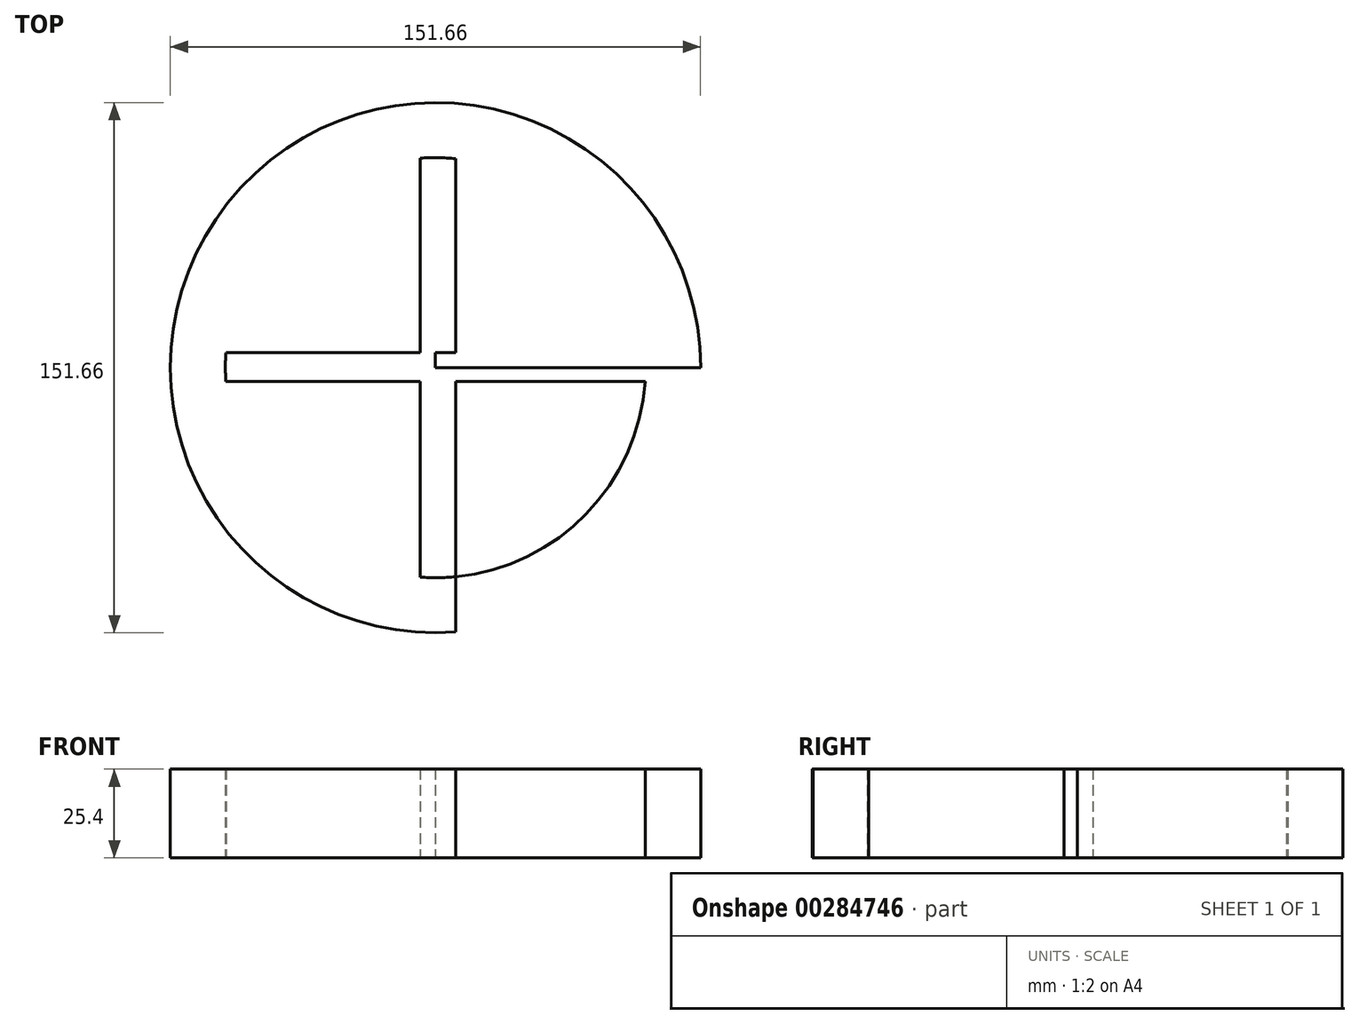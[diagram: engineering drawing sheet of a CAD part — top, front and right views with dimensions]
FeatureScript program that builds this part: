
annotation { "Feature Type Name" : "Feature", "Feature Type Description" : "" }
export const myFeature = defineFeature(function(context is Context, id is Id, definition is map)
    precondition{}
    {
        {
            var Q0;
            Q0=qCreatedBy(makeId("Top.planeOp"),FACE);
            var sketch = newSketch(context, id + "F0", { "sketchPlane" : qUnion([Q0])});
            skCircle(sketch, "E0", {"center": v(0, 0) * mm, "radius": 75.83 * mm});
            skCircle(sketch, "E1", {"center": v(0, 0) * mm, "radius": 60.08 * mm});
            skLineSegment(sketch, "E2", {"start": v(0, 0) * mm, "end": v(0, 75.83) * mm});
            skLineSegment(sketch, "E3", {"start": v(0, 75.83) * mm, "end": v(0, 0) * mm});
            skLineSegment(sketch, "E4", {"start": v(0, 0) * mm, "end": v(75.83, 0) * mm});
            skLineSegment(sketch, "E5", {"start": v(75.83, 0) * mm, "end": v(0, 0) * mm});
            skLineSegment(sketch, "E6", {"start": v(0, 4.36) * mm, "end": v(75.7, 4.36) * mm});
            skLineSegment(sketch, "E7", {"start": v(-4.36, 0) * mm, "end": v(-4.36, 75.83) * mm});
            skLineSegment(sketch, "E8", {"start": v(-4.36, 75.83) * mm, "end": v(-4.36, 0) * mm});
            skLineSegment(sketch, "E9", {"start": v(0, 0) * mm, "end": v(0, -75.83) * mm});
            skLineSegment(sketch, "E10", {"start": v(0, -75.83) * mm, "end": v(0, 0) * mm});
            skLineSegment(sketch, "E11", {"start": v(-4.36, 0) * mm, "end": v(-4.36, -75.7) * mm});
            skLineSegment(sketch, "E12", {"start": v(-4.36, -75.7) * mm, "end": v(-4.36, 0) * mm});
            skLineSegment(sketch, "E13", {"start": v(-4.36, 4.36) * mm, "end": v(-75.7, 4.36) * mm});
            skLineSegment(sketch, "E14", {"start": v(-75.7, 4.36) * mm, "end": v(-4.36, 4.36) * mm});
            skLineSegment(sketch, "E15", {"start": v(-4.36, 0) * mm, "end": v(-75.83, 0) * mm});
            skLineSegment(sketch, "E16", {"start": v(-75.83, 0) * mm, "end": v(-4.36, 0) * mm});
            skLineSegment(sketch, "E17", {"start": v(0, -3.88) * mm, "end": v(75.7, -3.88) * mm});
            skLineSegment(sketch, "E18", {"start": v(75.7, -3.88) * mm, "end": v(0, -3.88) * mm});
            skLineSegment(sketch, "E19", {"start": v(5.81, 0) * mm, "end": v(5.81, -75.6) * mm});
            skLineSegment(sketch, "E20", {"start": v(5.81, -75.6) * mm, "end": v(5.81, 0) * mm});
            skLineSegment(sketch, "E21", {"start": v(5.81, 4.36) * mm, "end": v(5.81, 75.6) * mm});
            skLineSegment(sketch, "E22", {"start": v(5.81, 75.6) * mm, "end": v(5.81, 4.36) * mm});
            skLineSegment(sketch, "E23", {"start": v(0, -3.88) * mm, "end": v(-75.83, -3.88) * mm});
            skLineSegment(sketch, "E24", {"start": v(-75.83, -3.88) * mm, "end": v(0, -3.88) * mm});
            skSolve(sketch);
        }
        {
            var Q0;
            {var subQ0=sQuery(id+"F0.wireOp",EDGE,"E12");var subQ1=sQuery(id+"F0.wireOp",EDGE,"E0");var subQ2=makeQuery(id+"F0.imprint","INTERSECT",VERTEX,{"derivedFrom":[subQ1,subQ0]});Q0=makeQuery(id+"F0.imprint","IMPRINT",FACE,{"disambiguationData":[TD([[makeQuery(id+"F0.imprint","IMPRINT",EDGE,{"disambiguationData":[TD([[subQ2,1.0]])],"derivedFrom":subQ1}),1.0]])]});}
            var Q1;
            {var subQ0=sQuery(id+"F0.wireOp",EDGE,"E14");var subQ1=sQuery(id+"F0.wireOp",EDGE,"E0");var subQ2=makeQuery(id+"F0.imprint","INTERSECT",VERTEX,{"derivedFrom":[subQ1,subQ0]});Q1=makeQuery(id+"F0.imprint","IMPRINT",FACE,{"disambiguationData":[TD([[makeQuery(id+"F0.imprint","IMPRINT",EDGE,{"disambiguationData":[TD([[subQ2,1.0]])],"derivedFrom":subQ1}),1.0]])]});}
            var Q2;
            {var subQ2=sQuery(id+"F0.wireOp",EDGE,"E1");var subQ5=sQuery(id+"F0.wireOp",EDGE,"E3");var subQ8=makeQuery(id+"F0.imprint","INTERSECT",VERTEX,{"derivedFrom":[subQ2,subQ5]});Q2=makeQuery(id+"F0.imprint","IMPRINT",FACE,{"disambiguationData":[TD([[makeQuery(id+"F0.imprint","IMPRINT",EDGE,{"disambiguationData":[TD([[subQ8,-1.0]])],"derivedFrom":subQ2}),1.0]])]});}
            var Q3;
            {var subQ0=sQuery(id+"F0.wireOp",EDGE,"E3");var subQ1=sQuery(id+"F0.wireOp",EDGE,"E0");var subQ2=makeQuery(id+"F0.imprint","INTERSECT",VERTEX,{"derivedFrom":[subQ1,subQ0]});Q3=makeQuery(id+"F0.imprint","IMPRINT",FACE,{"disambiguationData":[TD([[makeQuery(id+"F0.imprint","IMPRINT",EDGE,{"disambiguationData":[TD([[subQ2,1.0]])],"derivedFrom":subQ1}),1.0]])]});}
            var Q4;
            {var subQ0=sQuery(id+"F0.wireOp",EDGE,"E3");var subQ1=sQuery(id+"F0.wireOp",EDGE,"E0");var subQ2=makeQuery(id+"F0.imprint","INTERSECT",VERTEX,{"derivedFrom":[subQ1,subQ0]});Q4=makeQuery(id+"F0.imprint","IMPRINT",FACE,{"disambiguationData":[TD([[makeQuery(id+"F0.imprint","IMPRINT",EDGE,{"disambiguationData":[TD([[subQ2,-1.0]])],"derivedFrom":subQ1}),1.0]])]});}
            var Q5;
            {var subQ0=sQuery(id+"F0.wireOp",EDGE,"E22");var subQ1=sQuery(id+"F0.wireOp",EDGE,"E1");var subQ2=makeQuery(id+"F0.imprint","INTERSECT",VERTEX,{"derivedFrom":[subQ1,subQ0]});Q5=makeQuery(id+"F0.imprint","IMPRINT",FACE,{"disambiguationData":[TD([[makeQuery(id+"F0.imprint","IMPRINT",EDGE,{"disambiguationData":[TD([[subQ2,-1.0]])],"derivedFrom":subQ1}),1.0]])]});}
            var Q6;
            {var subQ4=sQuery(id+"F0.wireOp",EDGE,"E1");var subQ6=sQuery(id+"F0.wireOp",EDGE,"E6");var subQ8=makeQuery(id+"F0.imprint","INTERSECT",VERTEX,{"derivedFrom":[subQ4,subQ6]});Q6=makeQuery(id+"F0.imprint","IMPRINT",FACE,{"disambiguationData":[TD([[makeQuery(id+"F0.imprint","IMPRINT",EDGE,{"disambiguationData":[TD([[subQ8,1.0]])],"derivedFrom":subQ4}),1.0]])]});}
            var Q7;
            {var subQ1=sQuery(id+"F0.wireOp",EDGE,"E5");var subQ3=sQuery(id+"F0.wireOp",EDGE,"E20");var subQ4=makeQuery(id+"F0.imprint","INTERSECT",VERTEX,{"derivedFrom":[subQ1,subQ3]});Q7=makeQuery(id+"F0.imprint","IMPRINT",FACE,{"disambiguationData":[TD([[makeQuery(id+"F0.imprint","IMPRINT",EDGE,{"disambiguationData":[TD([[subQ4,1.0]])],"derivedFrom":subQ3}),1.0]])]});}
            var Q8;
            {var subQ2=sQuery(id+"F0.wireOp",EDGE,"E5");var subQ4=sQuery(id+"F0.wireOp",EDGE,"E0");var subQ5=makeQuery(id+"F0.imprint","INTERSECT",VERTEX,{"derivedFrom":[subQ4,subQ2]});Q8=makeQuery(id+"F0.imprint","IMPRINT",FACE,{"disambiguationData":[TD([[makeQuery(id+"F0.imprint","IMPRINT",EDGE,{"disambiguationData":[TD([[subQ5,1.0]])],"derivedFrom":subQ4}),1.0]])]});}
            var Q9;
            {var subQ0=sQuery(id+"F0.wireOp",EDGE,"E18");var subQ1=sQuery(id+"F0.wireOp",EDGE,"E1");var subQ2=makeQuery(id+"F0.imprint","INTERSECT",VERTEX,{"derivedFrom":[subQ1,subQ0]});Q9=makeQuery(id+"F0.imprint","IMPRINT",FACE,{"disambiguationData":[TD([[makeQuery(id+"F0.imprint","IMPRINT",EDGE,{"disambiguationData":[TD([[subQ2,-1.0]])],"derivedFrom":subQ1}),1.0]])]});}
            var Q10;
            {var subQ0=sQuery(id+"F0.wireOp",EDGE,"E6");var subQ1=sQuery(id+"F0.wireOp",EDGE,"E0");var subQ2=makeQuery(id+"F0.imprint","INTERSECT",VERTEX,{"derivedFrom":[subQ1,subQ0]});Q10=makeQuery(id+"F0.imprint","IMPRINT",FACE,{"disambiguationData":[TD([[makeQuery(id+"F0.imprint","IMPRINT",EDGE,{"disambiguationData":[TD([[subQ2,-1.0]])],"derivedFrom":subQ1}),1.0]])]});}
            var Q11;
            {var subQ0=sQuery(id+"F0.wireOp",EDGE,"E14");var subQ1=sQuery(id+"F0.wireOp",EDGE,"E0");var subQ2=makeQuery(id+"F0.imprint","INTERSECT",VERTEX,{"derivedFrom":[subQ1,subQ0]});Q11=makeQuery(id+"F0.imprint","IMPRINT",FACE,{"disambiguationData":[TD([[makeQuery(id+"F0.imprint","IMPRINT",EDGE,{"disambiguationData":[TD([[subQ2,-1.0]])],"derivedFrom":subQ1}),1.0]])]});}
            var Q12;
            {var subQ0=sQuery(id+"F0.wireOp",EDGE,"E16");var subQ1=sQuery(id+"F0.wireOp",EDGE,"E0");var subQ2=makeQuery(id+"F0.imprint","INTERSECT",VERTEX,{"derivedFrom":[subQ1,subQ0]});Q12=makeQuery(id+"F0.imprint","IMPRINT",FACE,{"disambiguationData":[TD([[makeQuery(id+"F0.imprint","IMPRINT",EDGE,{"disambiguationData":[TD([[subQ2,-1.0]])],"derivedFrom":subQ1}),1.0]])]});}
            var Q13;
            {var subQ0=sQuery(id+"F0.wireOp",EDGE,"E5");var subQ1=sQuery(id+"F0.wireOp",EDGE,"E0");var subQ2=makeQuery(id+"F0.imprint","INTERSECT",VERTEX,{"derivedFrom":[subQ1,subQ0]});Q13=makeQuery(id+"F0.imprint","IMPRINT",FACE,{"disambiguationData":[TD([[makeQuery(id+"F0.imprint","IMPRINT",EDGE,{"disambiguationData":[TD([[subQ2,-1.0]])],"derivedFrom":subQ1}),1.0]])]});}
            var Q14;
            {var subQ0=sQuery(id+"F0.wireOp",EDGE,"E16");var subQ1=sQuery(id+"F0.wireOp",EDGE,"E1");var subQ2=makeQuery(id+"F0.imprint","INTERSECT",VERTEX,{"derivedFrom":[subQ1,subQ0]});Q14=makeQuery(id+"F0.imprint","IMPRINT",FACE,{"disambiguationData":[TD([[makeQuery(id+"F0.imprint","IMPRINT",EDGE,{"disambiguationData":[TD([[subQ2,-1.0]])],"derivedFrom":subQ1}),1.0]])]});}
            var Q15;
            {var subQ0=sQuery(id+"F0.wireOp",EDGE,"E14");var subQ1=sQuery(id+"F0.wireOp",EDGE,"E1");var subQ2=makeQuery(id+"F0.imprint","INTERSECT",VERTEX,{"derivedFrom":[subQ1,subQ0]});Q15=makeQuery(id+"F0.imprint","IMPRINT",FACE,{"disambiguationData":[TD([[makeQuery(id+"F0.imprint","IMPRINT",EDGE,{"disambiguationData":[TD([[subQ2,-1.0]])],"derivedFrom":subQ1}),1.0]])]});}
            var Q16;
            {var subQ0=sQuery(id+"F0.wireOp",EDGE,"E12");var subQ1=sQuery(id+"F0.wireOp",EDGE,"E1");var subQ2=makeQuery(id+"F0.imprint","INTERSECT",VERTEX,{"derivedFrom":[subQ1,subQ0]});Q16=makeQuery(id+"F0.imprint","IMPRINT",FACE,{"disambiguationData":[TD([[makeQuery(id+"F0.imprint","IMPRINT",EDGE,{"disambiguationData":[TD([[subQ2,-1.0]])],"derivedFrom":subQ1}),1.0]])]});}
            var Q17;
            {var subQ0=sQuery(id+"F0.wireOp",EDGE,"E10");var subQ1=sQuery(id+"F0.wireOp",EDGE,"E1");var subQ2=makeQuery(id+"F0.imprint","INTERSECT",VERTEX,{"derivedFrom":[subQ1,subQ0]});Q17=makeQuery(id+"F0.imprint","IMPRINT",FACE,{"disambiguationData":[TD([[makeQuery(id+"F0.imprint","IMPRINT",EDGE,{"disambiguationData":[TD([[subQ2,-1.0]])],"derivedFrom":subQ1}),1.0]])]});}
            var Q18;
            {var subQ0=sQuery(id+"F0.wireOp",EDGE,"E10");var subQ1=sQuery(id+"F0.wireOp",EDGE,"E0");var subQ2=makeQuery(id+"F0.imprint","INTERSECT",VERTEX,{"derivedFrom":[subQ1,subQ0]});Q18=makeQuery(id+"F0.imprint","IMPRINT",FACE,{"disambiguationData":[TD([[makeQuery(id+"F0.imprint","IMPRINT",EDGE,{"disambiguationData":[TD([[subQ2,1.0]])],"derivedFrom":subQ1}),1.0]])]});}
            var Q19;
            {var subQ0=sQuery(id+"F0.wireOp",EDGE,"E10");var subQ1=sQuery(id+"F0.wireOp",EDGE,"E0");var subQ2=makeQuery(id+"F0.imprint","INTERSECT",VERTEX,{"derivedFrom":[subQ1,subQ0]});Q19=makeQuery(id+"F0.imprint","IMPRINT",FACE,{"disambiguationData":[TD([[makeQuery(id+"F0.imprint","IMPRINT",EDGE,{"disambiguationData":[TD([[subQ2,-1.0]])],"derivedFrom":subQ1}),1.0]])]});}
            extrude(context, id + "F1", {"entities" : qUnion([Q0, Q1, Q2, Q3, Q4, Q5, Q6, Q7, Q8, Q9, Q10, Q11, Q12, Q13, Q14, Q15, Q16, Q17, Q18, Q19]), "depth" : 25.4 * mm});
        }
    });
